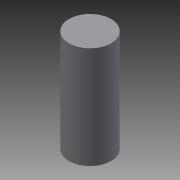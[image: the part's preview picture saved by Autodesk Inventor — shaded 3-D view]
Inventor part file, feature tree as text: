
AUTODESK INVENTOR PART (.ipt)
format: ipt  version: 2013 (Build 170138000, 138)  size: 77,824 bytes
history: native  units: mm
features: extrude x1, sketch x1
ambient origin geometry x8: Origin, YZ Plane, XZ Plane, XY Plane, X Axis, Y Axis, Z Axis, Center Point
bodies: Solid1 (feature_tree)
feature tree (2):
  extrude  "Extrusion1"  TaperAngle=0.0deg  [1 undecoded]
  sketch  "Sketch1"  dims[d2=0.0mm d3=0.0mm d4=0.0mm d9=0.0mm d10=0.0mm]
note: 1 required parameter value undecoded (feature->parameter linkage not recoverable at this tier; creation-order binding heuristic only, values carry confidence <= 0.55)
